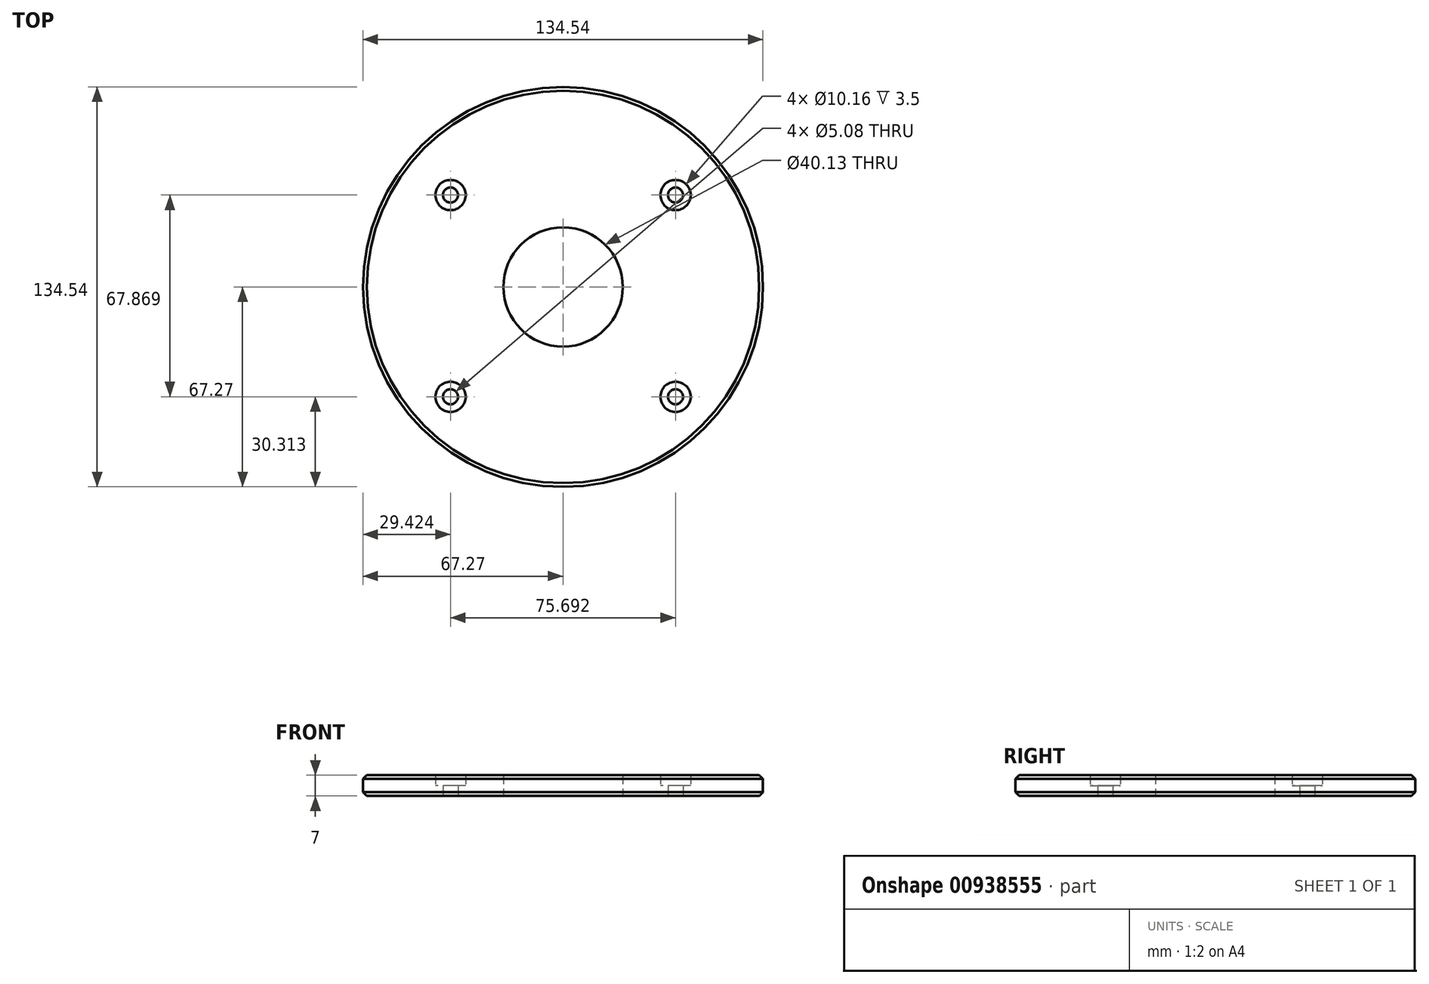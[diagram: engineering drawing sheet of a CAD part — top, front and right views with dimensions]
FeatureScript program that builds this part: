
annotation { "Feature Type Name" : "Feature", "Feature Type Description" : "" }
export const myFeature = defineFeature(function(context is Context, id is Id, definition is map)
    precondition{}
    {
        {
            assignVariable(context, id + "F0", {"name" : "plateThickness", "anyValue" : 7 * mm});
        }
        {
            var Q0;
            Q0=qCreatedBy(makeId("Top.planeOp"),FACE);
            var sketch = newSketch(context, id + "F1", { "sketchPlane" : qUnion([Q0])});
            skCircle(sketch, "E0", {"center": v(0, 0) * mm, "radius": 20.07 * mm});
            skLineSegment(sketch, "E1", {"start": v(48, -47.12) * mm, "end": v(-48, -47.12) * mm});
            skLineSegment(sketch, "E2", {"start": v(-48, -47.12) * mm, "end": v(-48, 41.07) * mm});
            skLineSegment(sketch, "E3", {"start": v(-48, 41.07) * mm, "end": v(-15.37, 41.07) * mm});
            skLineSegment(sketch, "E4", {"start": v(-15.37, 41.07) * mm, "end": v(-15.37, 37.13) * mm});
            skLineSegment(sketch, "E5", {"start": v(-15.37, 37.13) * mm, "end": v(15.37, 37.13) * mm});
            skLineSegment(sketch, "E6", {"start": v(15.37, 37.13) * mm, "end": v(15.37, 41.07) * mm});
            skLineSegment(sketch, "E7", {"start": v(15.37, 41.07) * mm, "end": v(48, 41.07) * mm});
            skLineSegment(sketch, "E8", {"start": v(48, 41.07) * mm, "end": v(48, -47.12) * mm});
            skPoint(sketch, "E9", {"position": v(0, -47.12) * mm});
            skLineSegment(sketch, "E10.bottom", {"start": v(-37.85, 30.91) * mm, "end": v(37.85, 30.91) * mm, "construction": true});
            skLineSegment(sketch, "E10.top", {"start": v(-37.85, -36.96) * mm, "end": v(37.85, -36.96) * mm, "construction": true});
            skLineSegment(sketch, "E10.left", {"start": v(-37.85, 30.91) * mm, "end": v(-37.85, -36.96) * mm, "construction": true});
            skLineSegment(sketch, "E10.right", {"start": v(37.85, 30.91) * mm, "end": v(37.85, -36.96) * mm, "construction": true});
            skCircle(sketch, "E11", {"center": v(-37.85, -36.96) * mm, "radius": 2.54 * mm});
            skCircle(sketch, "E12", {"center": v(-37.85, 30.91) * mm, "radius": 2.54 * mm});
            skCircle(sketch, "E13", {"center": v(37.85, 30.91) * mm, "radius": 2.54 * mm});
            skCircle(sketch, "E14", {"center": v(37.85, -36.96) * mm, "radius": 2.54 * mm});
            skCircle(sketch, "E15", {"center": v(-37.85, 30.91) * mm, "radius": 5.08 * mm});
            skCircle(sketch, "E16", {"center": v(37.85, 30.91) * mm, "radius": 5.08 * mm});
            skCircle(sketch, "E17", {"center": v(37.85, -36.96) * mm, "radius": 5.08 * mm});
            skCircle(sketch, "E18", {"center": v(-37.85, -36.96) * mm, "radius": 5.08 * mm});
            skSolve(sketch);
        }
        {
            var Q0;
            Q0=qCreatedBy(makeId("Top.planeOp"),FACE);
            var sketch = newSketch(context, id + "F2", { "sketchPlane" : qUnion([Q0])});
            skCircle(sketch, "E19.0", {"center": v(0, 0) * mm, "radius": 20.07 * mm});
            skCircle(sketch, "E20.0", {"center": v(-37.85, 30.91) * mm, "radius": 2.54 * mm});
            skCircle(sketch, "E21.0", {"center": v(37.85, 30.91) * mm, "radius": 2.54 * mm});
            skCircle(sketch, "E22.0", {"center": v(37.85, -36.96) * mm, "radius": 2.54 * mm});
            skCircle(sketch, "E23.0", {"center": v(-37.85, -36.96) * mm, "radius": 2.54 * mm});
            skCircle(sketch, "E24.0", {"center": v(-37.85, 30.91) * mm, "radius": 5.08 * mm});
            skCircle(sketch, "E25.0", {"center": v(37.85, 30.91) * mm, "radius": 5.08 * mm});
            skCircle(sketch, "E26.0", {"center": v(37.85, -36.96) * mm, "radius": 5.08 * mm});
            skCircle(sketch, "E27.0", {"center": v(-37.85, -36.96) * mm, "radius": 5.08 * mm});
            skCircle(sketch, "E28", {"center": v(0, 0) * mm, "radius": 67.27 * mm});
            skLineSegment(sketch, "E29.0", {"start": v(-48, -47.12) * mm, "end": v(-48, 41.07) * mm, "construction": true});
            skLineSegment(sketch, "E30.0", {"start": v(-48, 41.07) * mm, "end": v(-15.37, 41.07) * mm, "construction": true});
            skLineSegment(sketch, "E31.0", {"start": v(15.37, 41.07) * mm, "end": v(48, 41.07) * mm, "construction": true});
            skLineSegment(sketch, "E32.0", {"start": v(48, 41.07) * mm, "end": v(48, -47.12) * mm, "construction": true});
            skLineSegment(sketch, "E33.0", {"start": v(48, -47.12) * mm, "end": v(-48, -47.12) * mm, "construction": true});
            skSolve(sketch);
        }
        {
            var Q0;
            Q0=makeQuery(id+"F2.imprint","IMPRINT",FACE,{"disambiguationData":[TD([[makeQuery(id+"F2.imprint","IMPRINT",EDGE,{"derivedFrom":sQuery(id+"F2.wireOp",EDGE,"E19.0")}),-1.0]])]});
            extrude(context, id + "F3", {"entities" : qUnion([Q0]), "depth" : getVariable(context, 'plateThickness'), "offsetDistance" : 25.4 * mm});
        }
        {
            var Q0;
            Q0=makeQuery(id+"F1.imprint","IMPRINT",FACE,{"disambiguationData":[TD([[makeQuery(id+"F1.imprint","IMPRINT",EDGE,{"derivedFrom":sQuery(id+"F1.wireOp",EDGE,"E12")}),-1.0]])]});
            var Q1;
            Q1=makeQuery(id+"F1.imprint","IMPRINT",FACE,{"disambiguationData":[TD([[makeQuery(id+"F1.imprint","IMPRINT",EDGE,{"derivedFrom":sQuery(id+"F1.wireOp",EDGE,"E13")}),-1.0]])]});
            var Q2;
            Q2=makeQuery(id+"F1.imprint","IMPRINT",FACE,{"disambiguationData":[TD([[makeQuery(id+"F1.imprint","IMPRINT",EDGE,{"derivedFrom":sQuery(id+"F1.wireOp",EDGE,"E14")}),-1.0]])]});
            var Q3;
            Q3=makeQuery(id+"F1.imprint","IMPRINT",FACE,{"disambiguationData":[TD([[makeQuery(id+"F1.imprint","IMPRINT",EDGE,{"derivedFrom":sQuery(id+"F1.wireOp",EDGE,"E11")}),-1.0]])]});
            extrude(context, id + "F4", {"entities" : qUnion([Q0, Q1, Q2, Q3]), "operationType" : NewBodyOperationType.ADD, "depth" : getVariable(context, 'plateThickness') / 2, "offsetDistance" : 25.4 * mm});
        }
        {
            var Q0;
            Q0=makeQuery(id+"F3.opExtrude","CAP_EDGE",EDGE,{"disambiguationData":[OSD([sQuery(id+"F2.wireOp",EDGE,"E28")])],"isStart":true});
            var Q1;
            Q1=makeQuery(id+"F3.opExtrude","CAP_EDGE",EDGE,{"disambiguationData":[OSD([sQuery(id+"F2.wireOp",EDGE,"E28")])],"isStart":false});
            chamfer(context, id + "F5", {"entities" : qUnion([Q0, Q1]), "width" : 1.27 * mm, "tangentPropagation" : true});
        }
    });
